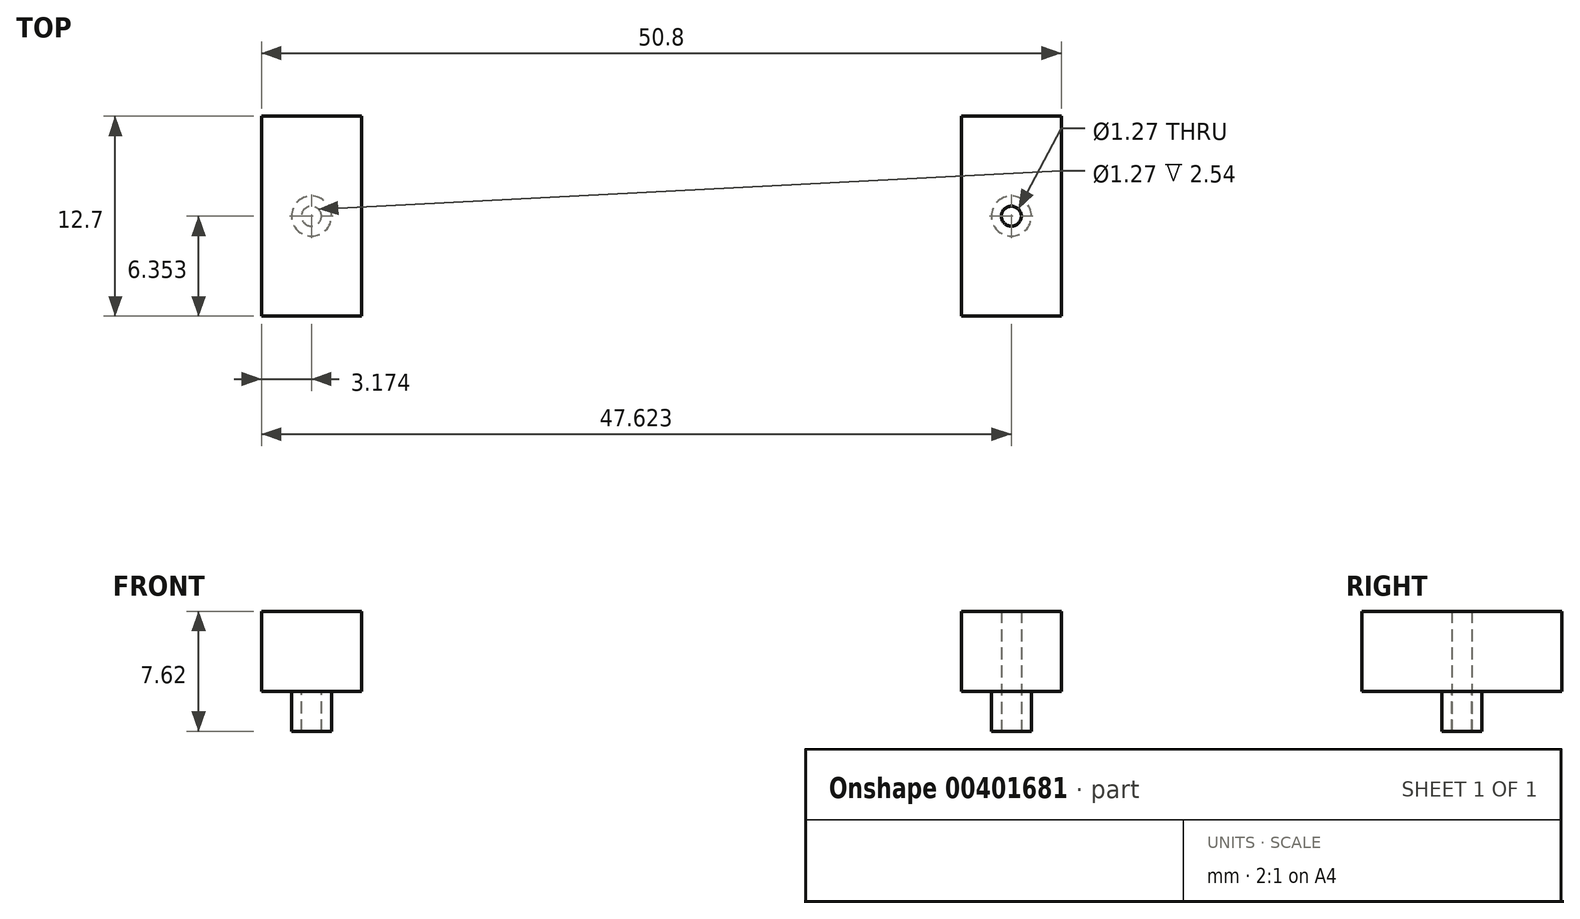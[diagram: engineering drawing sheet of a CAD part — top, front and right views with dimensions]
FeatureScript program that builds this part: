
annotation { "Feature Type Name" : "Feature", "Feature Type Description" : "" }
export const myFeature = defineFeature(function(context is Context, id is Id, definition is map)
    precondition{}
    {
        {
            var Q0;
            Q0=qCreatedBy(makeId("Top.planeOp"),FACE);
            var sketch = newSketch(context, id + "F0", { "sketchPlane" : qUnion([Q0])});
            skLineSegment(sketch, "E0.bottom", {"start": v(-27.25, -22.46) * mm, "end": v(23.55, -22.46) * mm});
            skLineSegment(sketch, "E0.top", {"start": v(-27.25, -35.16) * mm, "end": v(23.55, -35.16) * mm});
            skLineSegment(sketch, "E0.left", {"start": v(-27.25, -22.46) * mm, "end": v(-27.25, -35.16) * mm});
            skLineSegment(sketch, "E0.right", {"start": v(23.55, -22.46) * mm, "end": v(23.55, -35.16) * mm});
            skLineSegment(sketch, "E1", {"start": v(-27.25, -22.46) * mm, "end": v(-1.85, -22.46) * mm});
            skLineSegment(sketch, "E2", {"start": v(-1.85, -22.46) * mm, "end": v(-27.25, -22.46) * mm});
            skLineSegment(sketch, "E3", {"start": v(-14.55, -22.46) * mm, "end": v(-27.25, -22.46) * mm});
            skLineSegment(sketch, "E4", {"start": v(-20.9, -22.46) * mm, "end": v(-20.9, -35.16) * mm});
            skLineSegment(sketch, "E5", {"start": v(-20.9, -35.16) * mm, "end": v(-27.25, -22.46) * mm});
            skLineSegment(sketch, "E6", {"start": v(23.55, -22.46) * mm, "end": v(-1.85, -22.46) * mm});
            skLineSegment(sketch, "E7", {"start": v(10.85, -22.46) * mm, "end": v(23.55, -22.46) * mm});
            skLineSegment(sketch, "E8", {"start": v(17.2, -22.46) * mm, "end": v(17.2, -35.16) * mm});
            skLineSegment(sketch, "E9", {"start": v(17.2, -35.16) * mm, "end": v(23.55, -22.46) * mm});
            skLineSegment(sketch, "E10", {"start": v(-20.9, -35.16) * mm, "end": v(-24.08, -28.8) * mm});
            skLineSegment(sketch, "E11", {"start": v(20.37, -28.8) * mm, "end": v(23.55, -22.46) * mm});
            skCircle(sketch, "E12", {"center": v(-24.08, -28.8) * mm, "radius": 1.27 * mm});
            skCircle(sketch, "E13", {"center": v(20.37, -28.8) * mm, "radius": 1.27 * mm});
            skCircle(sketch, "E14", {"center": v(-24.08, -28.8) * mm, "radius": 0.64 * mm});
            skCircle(sketch, "E15", {"center": v(20.37, -28.8) * mm, "radius": 0.64 * mm});
            skSolve(sketch);
        }
        {
            var Q0;
            {var subQ1=sQuery(id+"F0.wireOp",EDGE,"E4");Q0=makeQuery(id+"F0.imprint","IMPRINT",FACE,{"disambiguationData":[TD([[makeQuery(id+"F0.imprint","IMPRINT",EDGE,{"derivedFrom":subQ1}),-1.0]])]});}
            var Q1;
            {var subQ6=sQuery(id+"F0.wireOp",EDGE,"E0.left");Q1=makeQuery(id+"F0.imprint","IMPRINT",FACE,{"disambiguationData":[TD([[makeQuery(id+"F0.imprint","IMPRINT",EDGE,{"derivedFrom":subQ6}),1.0]])]});}
            var Q2;
            {var subQ0=sQuery(id+"F0.wireOp",EDGE,"E10");var subQ1=sQuery(id+"F0.wireOp",EDGE,"E5");var subQ2=makeQuery(id+"F0.imprint","INTERSECT",VERTEX,{"derivedFrom":[subQ1,subQ0]});Q2=makeQuery(id+"F0.imprint","IMPRINT",FACE,{"disambiguationData":[TD([[makeQuery(id+"F0.imprint","IMPRINT",EDGE,{"disambiguationData":[TD([[subQ2,-1.0]])],"derivedFrom":subQ1}),-1.0]])]});}
            var Q3;
            {var subQ0=sQuery(id+"F0.wireOp",EDGE,"E10");var subQ1=sQuery(id+"F0.wireOp",EDGE,"E5");var subQ2=makeQuery(id+"F0.imprint","INTERSECT",VERTEX,{"derivedFrom":[subQ1,subQ0]});Q3=makeQuery(id+"F0.imprint","IMPRINT",FACE,{"disambiguationData":[TD([[makeQuery(id+"F0.imprint","IMPRINT",EDGE,{"disambiguationData":[TD([[subQ2,-1.0]])],"derivedFrom":subQ1}),1.0]])]});}
            var Q4;
            {var subQ0=sQuery(id+"F0.wireOp",EDGE,"E14");var subQ1=sQuery(id+"F0.wireOp",EDGE,"E5");var subQ2=makeQuery(id+"F0.imprint","INTERSECT",VERTEX,{"derivedFrom":[subQ1,subQ0]});Q4=makeQuery(id+"F0.imprint","IMPRINT",FACE,{"disambiguationData":[TD([[makeQuery(id+"F0.imprint","IMPRINT",EDGE,{"disambiguationData":[TD([[subQ2,-1.0]])],"derivedFrom":subQ1}),1.0]])]});}
            var Q5;
            {var subQ0=sQuery(id+"F0.wireOp",EDGE,"E14");var subQ1=sQuery(id+"F0.wireOp",EDGE,"E5");var subQ2=makeQuery(id+"F0.imprint","INTERSECT",VERTEX,{"derivedFrom":[subQ1,subQ0]});Q5=makeQuery(id+"F0.imprint","IMPRINT",FACE,{"disambiguationData":[TD([[makeQuery(id+"F0.imprint","IMPRINT",EDGE,{"disambiguationData":[TD([[subQ2,-1.0]])],"derivedFrom":subQ1}),-1.0]])]});}
            var Q6;
            {var subQ1=sQuery(id+"F0.wireOp",EDGE,"E2");Q6=makeQuery(id+"F0.imprint","IMPRINT",FACE,{"disambiguationData":[TD([[makeQuery(id+"F0.imprint","IMPRINT",EDGE,{"derivedFrom":subQ1}),1.0]])]});}
            var Q7;
            {var subQ0=sQuery(id+"F0.wireOp",EDGE,"E11");var subQ1=sQuery(id+"F0.wireOp",EDGE,"E9");var subQ2=makeQuery(id+"F0.imprint","INTERSECT",VERTEX,{"derivedFrom":[subQ1,subQ0]});Q7=makeQuery(id+"F0.imprint","IMPRINT",FACE,{"disambiguationData":[TD([[makeQuery(id+"F0.imprint","IMPRINT",EDGE,{"disambiguationData":[TD([[subQ2,1.0]])],"derivedFrom":subQ1}),-1.0]])]});}
            var Q8;
            {var subQ0=sQuery(id+"F0.wireOp",EDGE,"E11");var subQ1=sQuery(id+"F0.wireOp",EDGE,"E9");var subQ2=makeQuery(id+"F0.imprint","INTERSECT",VERTEX,{"derivedFrom":[subQ1,subQ0]});Q8=makeQuery(id+"F0.imprint","IMPRINT",FACE,{"disambiguationData":[TD([[makeQuery(id+"F0.imprint","IMPRINT",EDGE,{"disambiguationData":[TD([[subQ2,1.0]])],"derivedFrom":subQ1}),1.0]])]});}
            var Q9;
            {var subQ0=sQuery(id+"F0.wireOp",EDGE,"E13");var subQ1=sQuery(id+"F0.wireOp",EDGE,"E9");var subQ2=makeQuery(id+"F0.imprint","INTERSECT",VERTEX,{"derivedFrom":[subQ1,subQ0]});Q9=makeQuery(id+"F0.imprint","IMPRINT",FACE,{"disambiguationData":[TD([[makeQuery(id+"F0.imprint","IMPRINT",EDGE,{"disambiguationData":[TD([[subQ2,-1.0]])],"derivedFrom":subQ1}),1.0]])]});}
            var Q10;
            {var subQ0=sQuery(id+"F0.wireOp",EDGE,"E13");var subQ1=sQuery(id+"F0.wireOp",EDGE,"E9");var subQ2=makeQuery(id+"F0.imprint","INTERSECT",VERTEX,{"derivedFrom":[subQ1,subQ0]});Q10=makeQuery(id+"F0.imprint","IMPRINT",FACE,{"disambiguationData":[TD([[makeQuery(id+"F0.imprint","IMPRINT",EDGE,{"disambiguationData":[TD([[subQ2,-1.0]])],"derivedFrom":subQ1}),-1.0]])]});}
            var Q11;
            {var subQ6=sQuery(id+"F0.wireOp",EDGE,"E0.right");Q11=makeQuery(id+"F0.imprint","IMPRINT",FACE,{"disambiguationData":[TD([[makeQuery(id+"F0.imprint","IMPRINT",EDGE,{"derivedFrom":subQ6}),-1.0]])]});}
            var Q12;
            {var subQ1=sQuery(id+"F0.wireOp",EDGE,"E8");Q12=makeQuery(id+"F0.imprint","IMPRINT",FACE,{"disambiguationData":[TD([[makeQuery(id+"F0.imprint","IMPRINT",EDGE,{"derivedFrom":subQ1}),1.0]])]});}
            extrude(context, id + "F1", {"entities" : qUnion([Q0, Q1, Q2, Q3, Q4, Q5, Q6, Q7, Q8, Q9, Q10, Q11, Q12]), "depth" : 5.08 * mm});
        }
        {
            var Q0;
            Q0=makeQuery(id+"F1.opExtrude","CAP_FACE",FACE,{"disambiguationData":[OSD([sQuery(id+"F0.wireOp",EDGE,"E0.top"),sQuery(id+"F0.wireOp",EDGE,"E0.left"),sQuery(id+"F0.wireOp",EDGE,"E0.right"),sQuery(id+"F0.wireOp",EDGE,"E2"),sQuery(id+"F0.wireOp",EDGE,"E3"),sQuery(id+"F0.wireOp",EDGE,"E6"),sQuery(id+"F0.wireOp",EDGE,"E7")])],"isStart":true});
            var sketch = newSketch(context, id + "F2", { "sketchPlane" : qUnion([Q0])});
            skLineSegment(sketch, "E16", {"start": v(-27.25, 22.46) * mm, "end": v(-27.25, 35.16) * mm});
            skLineSegment(sketch, "E17", {"start": v(-27.25, 35.16) * mm, "end": v(-1.85, 35.16) * mm});
            skLineSegment(sketch, "E18", {"start": v(-1.85, 35.16) * mm, "end": v(-14.55, 35.16) * mm});
            skLineSegment(sketch, "E19", {"start": v(-14.55, 35.16) * mm, "end": v(-27.25, 35.16) * mm});
            skLineSegment(sketch, "E20", {"start": v(-20.9, 35.16) * mm, "end": v(-20.9, 22.46) * mm});
            skLineSegment(sketch, "E21", {"start": v(-20.9, 22.46) * mm, "end": v(-27.25, 35.16) * mm});
            skLineSegment(sketch, "E22", {"start": v(-27.25, 35.16) * mm, "end": v(-24.08, 28.8) * mm});
            skLineSegment(sketch, "E23", {"start": v(-1.85, 35.16) * mm, "end": v(23.55, 35.16) * mm});
            skLineSegment(sketch, "E24", {"start": v(23.55, 35.16) * mm, "end": v(10.85, 35.16) * mm});
            skLineSegment(sketch, "E25", {"start": v(10.85, 35.16) * mm, "end": v(17.2, 35.16) * mm});
            skLineSegment(sketch, "E26", {"start": v(17.2, 35.16) * mm, "end": v(17.2, 22.46) * mm});
            skLineSegment(sketch, "E27", {"start": v(17.2, 35.16) * mm, "end": v(23.55, 22.46) * mm});
            skLineSegment(sketch, "E28", {"start": v(23.55, 22.46) * mm, "end": v(20.37, 28.8) * mm});
            skCircle(sketch, "E29", {"center": v(-24.08, 28.8) * mm, "radius": 1.27 * mm});
            skCircle(sketch, "E30", {"center": v(20.37, 28.8) * mm, "radius": 1.27 * mm});
            skCircle(sketch, "E31", {"center": v(-24.08, 28.8) * mm, "radius": 0.64 * mm});
            skCircle(sketch, "E32", {"center": v(20.37, 28.8) * mm, "radius": 0.64 * mm});
            skSolve(sketch);
        }
        {
            var Q0;
            {var subQ0=sQuery(id+"F2.wireOp",EDGE,"E29");var subQ1=sQuery(id+"F2.wireOp",EDGE,"E21");var subQ2=makeQuery(id+"F2.imprint","INTERSECT",VERTEX,{"derivedFrom":[subQ1,subQ0]});Q0=makeQuery(id+"F2.imprint","IMPRINT",FACE,{"disambiguationData":[TD([[makeQuery(id+"F2.imprint","IMPRINT",EDGE,{"disambiguationData":[TD([[subQ2,-1.0]])],"derivedFrom":subQ1}),-1.0]])]});}
            var Q1;
            {var subQ0=sQuery(id+"F2.wireOp",EDGE,"E29");var subQ1=sQuery(id+"F2.wireOp",EDGE,"E21");var subQ2=makeQuery(id+"F2.imprint","INTERSECT",VERTEX,{"derivedFrom":[subQ1,subQ0]});Q1=makeQuery(id+"F2.imprint","IMPRINT",FACE,{"disambiguationData":[TD([[makeQuery(id+"F2.imprint","IMPRINT",EDGE,{"disambiguationData":[TD([[subQ2,-1.0]])],"derivedFrom":subQ1}),1.0]])]});}
            var Q2;
            {var subQ0=sQuery(id+"F2.wireOp",EDGE,"E30");var subQ1=sQuery(id+"F2.wireOp",EDGE,"E27");var subQ2=makeQuery(id+"F2.imprint","INTERSECT",VERTEX,{"derivedFrom":[subQ1,subQ0]});Q2=makeQuery(id+"F2.imprint","IMPRINT",FACE,{"disambiguationData":[TD([[makeQuery(id+"F2.imprint","IMPRINT",EDGE,{"disambiguationData":[TD([[subQ2,-1.0]])],"derivedFrom":subQ1}),-1.0]])]});}
            var Q3;
            {var subQ0=sQuery(id+"F2.wireOp",EDGE,"E30");var subQ1=sQuery(id+"F2.wireOp",EDGE,"E27");var subQ2=makeQuery(id+"F2.imprint","INTERSECT",VERTEX,{"derivedFrom":[subQ1,subQ0]});Q3=makeQuery(id+"F2.imprint","IMPRINT",FACE,{"disambiguationData":[TD([[makeQuery(id+"F2.imprint","IMPRINT",EDGE,{"disambiguationData":[TD([[subQ2,-1.0]])],"derivedFrom":subQ1}),1.0]])]});}
            extrude(context, id + "F3", {"entities" : qUnion([Q0, Q1, Q2, Q3]), "operationType" : NewBodyOperationType.ADD, "depth" : 2.54 * mm});
        }
    });
